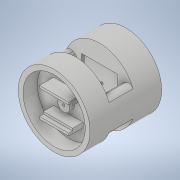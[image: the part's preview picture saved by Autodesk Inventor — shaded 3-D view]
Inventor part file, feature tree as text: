
AUTODESK INVENTOR PART (.ipt)
format: ipt  version: 2020 (Build 240168000, 168)  size: 382,976 bytes
history: native  units: mm
features: extrude x17, sketch x12, other x3, projected_geometry x2, plane x1, mirror x1, fillet x1
ambient origin geometry x8: Origin, YZ Plane, XZ Plane, XY Plane, X Axis, Y Axis, Z Axis, Center Point
bodies: Volumenkörper1 (feature_tree)
feature tree (37):
  extrude  "Grundkörper"  Depth=30.0mm TaperAngle=0.0deg
  plane  "Arbeitsebene1"
  extrude  "Ausschnitt Medienfluss"  Depth=20.0mm
  extrude  "Ausschnitt Einlage Glas"  TaperAngle=30.0deg  [1 undecoded]
  extrude  "Wandung Grundkörper"  Depth=20.0mm TaperAngle=360.0deg
  extrude  "Ausschnitt Strahlengang"  Depth=5.0mm TaperAngle=0.0deg
  mirror  "Spiegeln Wandung und Stahlengang"
  other  "Lage Detektor"
  extrude  "Kabelgang von LED"  Depth=15.0mm
  fillet  "Rundung Kabelgang von LED"  Radius=7.5mm
  other  "Lage LED"
  extrude  "Halterung LED"  Depth=6.0mm TaperAngle=0.0deg
  extrude  "Auflage LED"  Depth=7.0mm TaperAngle=0.0deg
  extrude  "Kabelabführung LED"  Depth=7.0mm TaperAngle=0.0deg
  extrude  "Abnahme für Halbkugel"  TaperAngle=90.0deg  [1 undecoded]
  extrude  "Nut"  Depth=16.51mm
  extrude  "Extrusion15"  Depth=16.51mm
  extrude  "Blende"  Depth=26.0mm
  extrude  "Extrusion16"  TaperAngle=165.0deg  [1 undecoded]
  extrude  "Extrusion17"  Depth=25.0mm
  extrude  "Ausschnitt Detektor"  Depth=1.0mm
  extrude  "Auflage Detektor"  Depth=1.0mm
  sketch  "Skizze1"  dims[d0=30.0mm d1=30.0mm d2=0.0mm]
  sketch  "Skizze2"  dims[d3=30.0mm d4=20.0mm]
  other  "Lage Ausschnitt Sichtglas"
  sketch  "Skizze4"  dims[d5=30.0deg d7=30.0deg]
  sketch  "Skizze5"  dims[d8=2.0mm d9=20.0mm d11=360.0deg]
  sketch  "Skizze7"  dims[d13=30.0mm d14=5.0mm d15=5.0mm d16=0.0mm d17=0.0mm]
  sketch  "Skizze9"  dims[d18=15.0mm d19=15.0mm d20=7.5mm]
  sketch  "Skizze10"  dims[d21=7.5mm d22=6.0mm d23=6.0mm d24=0.0mm d25=0.0mm]
  sketch  "Skizze11"  dims[d26=26.0mm d27=7.0mm d28=0.0mm]
  projected_geometry  "Projizierte Kontur1"
  sketch  "Skizze12"  dims[d29=1.0mm d30=7.0mm d31=0.0mm]
  sketch  "Skizze13"  dims[d32=9.398mm d33=90.0deg]
  sketch  "Skizze14"  dims[d34=9.398mm d35=16.51mm]
  sketch  "Skizze15"  dims[d37=19.05mm d39=16.51mm d41=26.0mm d52=165.0deg d63=25.0mm d65=1.0mm d66=1.0mm d67=1.745329mm d68=1.745329mm d69=12.0mm d70=8.0mm d71=0.0mm d72=0.0mm d73=2.0mm d74=10.2mm d75=10.2mm d76=5.1mm d77=5.1mm d78=1.0mm d79=1.0mm d80=6.0mm d81=0.0mm d82=4.4mm d83=0.0mm d84=1.0mm d85=5.0mm d86=2.0mm d87=0.0mm d88=5.0mm d89=2.0mm d90=0.0mm d91=1.0mm d92=0.0mm d93=0.95mm d94=1.0mm d95=0.0mm d96=10.0mm d97=0.0mm d98=10.0mm d99=0.0mm d101=6.0mm d102=0.0mm d105=7.25mm d106=0.0mm d107=2.0mm d108=0.0mm]
  projected_geometry  "Projizierte Kontur2"
note: 3 required parameter values undecoded (feature->parameter linkage not recoverable at this tier; creation-order binding heuristic only, values carry confidence <= 0.55)
